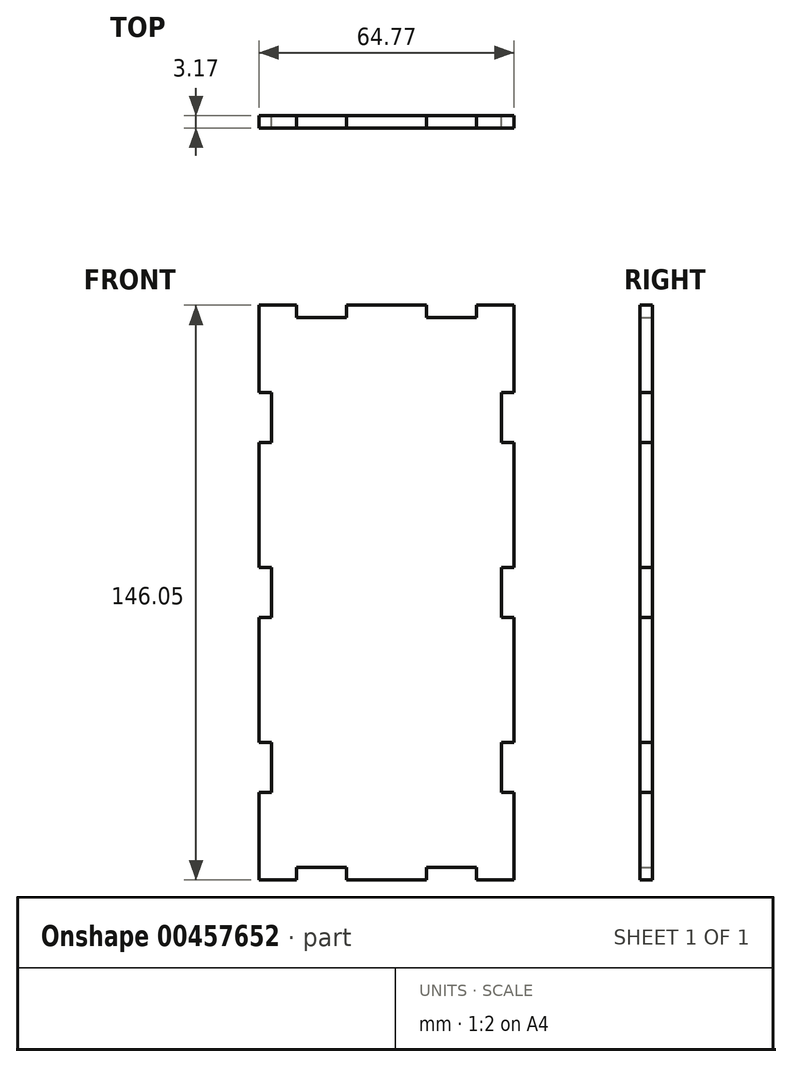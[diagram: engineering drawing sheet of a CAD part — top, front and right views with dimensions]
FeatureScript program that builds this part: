
annotation { "Feature Type Name" : "Feature", "Feature Type Description" : "" }
export const myFeature = defineFeature(function(context is Context, id is Id, definition is map)
    precondition{}
    {
        {
            var Q0;
            Q0=qCreatedBy(makeId("Front.planeOp"),FACE);
            var sketch = newSketch(context, id + "F0", { "sketchPlane" : qUnion([Q0])});
            skPoint(sketch, "E0.middle", {"position": v(0, 0) * mm});
            skLineSegment(sketch, "E1.bottom", {"start": v(-31.27, 51.43) * mm, "end": v(-28.1, 51.43) * mm});
            skLineSegment(sketch, "E1.top", {"start": v(-31.27, 38.73) * mm, "end": v(-28.1, 38.73) * mm});
            skLineSegment(sketch, "E1.right", {"start": v(-28.1, 51.43) * mm, "end": v(-28.1, 38.73) * mm});
            skLineSegment(sketch, "E2.bottom", {"start": v(-31.27, -37.46) * mm, "end": v(-28.1, -37.46) * mm});
            skLineSegment(sketch, "E2.top", {"start": v(-31.27, -50.16) * mm, "end": v(-28.1, -50.16) * mm});
            skLineSegment(sketch, "E2.right", {"start": v(-28.1, -37.46) * mm, "end": v(-28.1, -50.16) * mm});
            skLineSegment(sketch, "E3.bottom", {"start": v(30.33, -37.46) * mm, "end": v(33.5, -37.46) * mm});
            skLineSegment(sketch, "E3.top", {"start": v(30.33, -50.16) * mm, "end": v(33.5, -50.16) * mm});
            skLineSegment(sketch, "E3.left", {"start": v(30.33, -37.46) * mm, "end": v(30.33, -50.16) * mm});
            skLineSegment(sketch, "E4.bottom", {"start": v(-31.27, 6.99) * mm, "end": v(-28.1, 6.99) * mm});
            skLineSegment(sketch, "E4.top", {"start": v(-31.27, -5.71) * mm, "end": v(-28.1, -5.71) * mm});
            skLineSegment(sketch, "E4.right", {"start": v(-28.1, 6.99) * mm, "end": v(-28.1, -5.71) * mm});
            skLineSegment(sketch, "E5.top", {"start": v(-21.74, 70.48) * mm, "end": v(-9.04, 70.48) * mm});
            skLineSegment(sketch, "E5.left", {"start": v(-21.74, 73.66) * mm, "end": v(-21.74, 70.48) * mm});
            skLineSegment(sketch, "E5.right", {"start": v(-9.04, 73.66) * mm, "end": v(-9.04, 70.48) * mm});
            skLineSegment(sketch, "E6.bottom", {"start": v(30.33, 6.99) * mm, "end": v(33.5, 6.99) * mm});
            skLineSegment(sketch, "E6.top", {"start": v(30.33, -5.71) * mm, "end": v(33.5, -5.71) * mm});
            skLineSegment(sketch, "E6.left", {"start": v(30.33, 6.99) * mm, "end": v(30.33, -5.71) * mm});
            skLineSegment(sketch, "E7.bottom", {"start": v(30.33, 51.44) * mm, "end": v(33.5, 51.44) * mm});
            skLineSegment(sketch, "E7.top", {"start": v(30.33, 38.74) * mm, "end": v(33.5, 38.74) * mm});
            skLineSegment(sketch, "E7.left", {"start": v(30.33, 51.44) * mm, "end": v(30.33, 38.74) * mm});
            skLineSegment(sketch, "E7.right", {"start": v(33.5, 73.66) * mm, "end": v(33.5, 51.44) * mm});
            skLineSegment(sketch, "E8.top", {"start": v(11.28, 70.48) * mm, "end": v(23.98, 70.48) * mm});
            skLineSegment(sketch, "E8.left", {"start": v(11.28, 73.66) * mm, "end": v(11.28, 70.48) * mm});
            skLineSegment(sketch, "E8.right", {"start": v(23.98, 73.66) * mm, "end": v(23.98, 70.48) * mm});
            skLineSegment(sketch, "E9.bottom", {"start": v(-21.74, -69.21) * mm, "end": v(-9.04, -69.21) * mm});
            skLineSegment(sketch, "E9.top", {"start": v(-31.27, -72.39) * mm, "end": v(-21.74, -72.39) * mm});
            skLineSegment(sketch, "E9.left", {"start": v(-21.74, -69.21) * mm, "end": v(-21.74, -72.39) * mm});
            skLineSegment(sketch, "E9.right", {"start": v(-9.04, -69.21) * mm, "end": v(-9.04, -72.39) * mm});
            skLineSegment(sketch, "E10.bottom", {"start": v(11.28, -69.21) * mm, "end": v(23.98, -69.21) * mm});
            skLineSegment(sketch, "E10.left", {"start": v(11.28, -69.21) * mm, "end": v(11.28, -72.39) * mm});
            skLineSegment(sketch, "E10.right", {"start": v(23.98, -69.21) * mm, "end": v(23.98, -72.39) * mm});
            skLineSegment(sketch, "E11", {"start": v(11.28, 73.66) * mm, "end": v(-9.04, 73.66) * mm});
            skLineSegment(sketch, "E12", {"start": v(23.98, 73.66) * mm, "end": v(33.5, 73.66) * mm});
            skLineSegment(sketch, "E13", {"start": v(-21.74, 73.66) * mm, "end": v(-31.27, 73.66) * mm});
            skLineSegment(sketch, "E14", {"start": v(-31.27, 51.43) * mm, "end": v(-31.27, 73.66) * mm});
            skLineSegment(sketch, "E15", {"start": v(-31.27, 38.73) * mm, "end": v(-31.27, 6.99) * mm});
            skLineSegment(sketch, "E16", {"start": v(-31.27, -50.16) * mm, "end": v(-31.27, -72.39) * mm});
            skLineSegment(sketch, "E17", {"start": v(-31.27, -5.71) * mm, "end": v(-31.27, -37.46) * mm});
            skLineSegment(sketch, "E18.trimOffspring", {"start": v(33.5, -5.71) * mm, "end": v(33.5, -37.46) * mm});
            skLineSegment(sketch, "E19.trimOffspring", {"start": v(33.5, -50.16) * mm, "end": v(33.5, -72.39) * mm});
            skLineSegment(sketch, "E20.trimOffspring", {"start": v(33.5, 38.74) * mm, "end": v(33.5, 6.99) * mm});
            skLineSegment(sketch, "E21.trimOffspring", {"start": v(23.98, -72.39) * mm, "end": v(33.5, -72.39) * mm});
            skLineSegment(sketch, "E22.trimOffspring", {"start": v(-9.04, -72.39) * mm, "end": v(11.28, -72.39) * mm});
            skSolve(sketch);
        }
        {
            var Q0;
            Q0 = qSketchRegion(id + "F0", true);
            var Q1;
            Q1=makeQuery(id+"F0.imprint","IMPRINT",FACE,{"disambiguationData":[TD([[makeQuery(id+"F0.imprint","IMPRINT",EDGE,{"derivedFrom":sQuery(id+"F0.wireOp",EDGE,"ezhVGio5-4wVQ-Yd38-8q68-diiR05VLwqXW.bottom")}),-1.0]])]});
            extrude(context, id + "F1", {"entities" : qUnion([Q0, Q1]), "depth" : 3.17 * mm});
        }
    });
